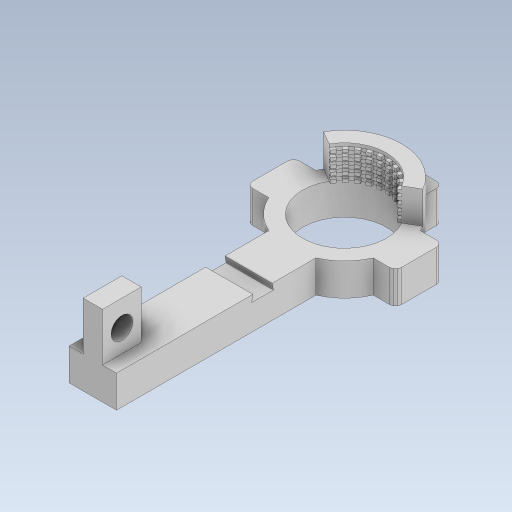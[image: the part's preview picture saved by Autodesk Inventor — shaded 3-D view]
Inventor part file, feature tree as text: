
AUTODESK INVENTOR PART (.ipt)
format: ipt  version: 2023 (Build 270158000, 158)  size: 442,880 bytes
history: native  units: in
note: dims shown in document units (in); Inventor stores cm internally (conversion verified against a paired STEP export)
features: sketch x8, extrude x6, revolve x1, hole x1
ambient origin geometry x8: Origin, YZ Plane, XZ Plane, XY Plane, X Axis, Y Axis, Z Axis, Center Point
bodies: Solid1 (feature_tree)
feature tree (16):
  extrude  "Extrusion1"  Depth=0.3937in TaperAngle=0.0deg
  extrude  "Extrusion2"  Depth=0.3937in TaperAngle=0.0deg
  extrude  "Extrusion3"  Depth=0.0394in TaperAngle=120.0deg
  revolve  "Revolution1"  [1 undecoded]
  extrude  "Extrusion4"  Depth=0.1969in TaperAngle=0.0deg
  extrude  "Extrusion5"  Depth=0.2362in
  extrude  "Extrusion6"  Depth=0.0787in
  hole  "Hole1"  [1 undecoded]
  sketch  "Sketch1"  dims[d0=1.0236in d1=0.3937in d2=0.0in]
  sketch  "Sketch2"  dims[d3=120.0deg d4=0.3937in d5=0.0in]
  sketch  "Sketch3"  dims[d6=0.0394in d7=7.874in d9=120.0deg]
  sketch  "Sketch4"  dims[d11=0.3937in d12=0.0in d14=3.937in d16=0.0394in d17=0.3937in d19=0.3937in]
  sketch  "Sketch5"  dims[d21=360.0deg d22=2.1654in d23=0.1969in d24=0.0in d25=0.0in]
  sketch  "Sketch6"  dims[d26=0.2362in d27=1.1723in]
  sketch  "Sketch7"  dims[d28=1.3998in d29=0.0787in d30=0.0687in]
  sketch  "Sketch8"  dims[d31=0.2362in d32=0.4724in d33=0.5906in d34=0.0in d35=0.2756in d36=0.266in d37=0.2362in d38=0.1575in d39=0.0787in d40=90.0deg d41=0.315in d42=0.8108in]
note: 2 required parameter values undecoded (feature->parameter linkage not recoverable at this tier; creation-order binding heuristic only, values carry confidence <= 0.55)